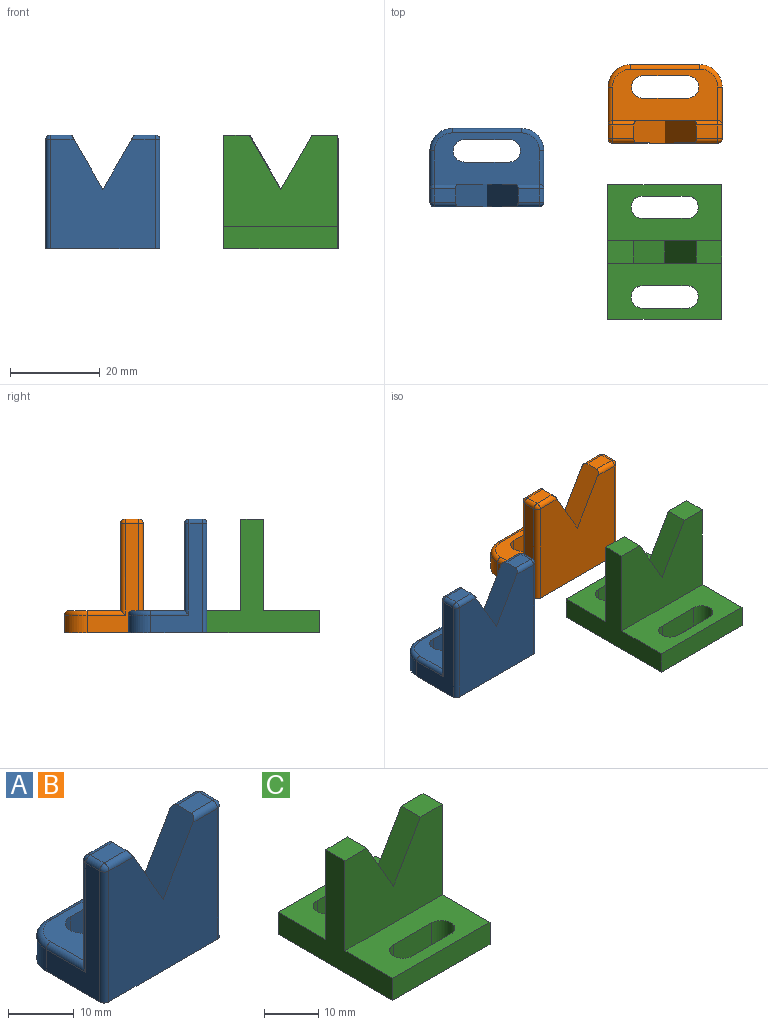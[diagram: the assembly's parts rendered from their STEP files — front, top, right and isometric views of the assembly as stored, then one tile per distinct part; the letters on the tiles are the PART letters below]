
ASSEMBLY  parts=3 mates=2
PART A: 36 faces, bbox 26.2x17.9x25.4 mm
  f0: plane 24.4x11.5mm, normal (-1,0,0), area 107.2mm2, adj f1,f12,f18,f21,f23,f26
  f1: plane 25.4x17.5mm, normal (0,0,-1), area 363.7mm2, adj f0,f2,f7,f9,f10,f11,f12,f13
  f2: plane 24.4x11.5mm, normal (1,0,0), area 107.2mm2, adj f1,f14,f24,f29,f34,f35
  f3: plane 4.72x3mm, normal (0,0,1), area 14.1mm2, adj f4,f25,f29,f30
  f4: plane 12.1x6.99mm, normal (-0.87,0,0.5), area 69.4mm2, adj f3,f5,f7,f8,f25,f30
  f5: plane 12.1x6.99mm, normal (0.87,0,0.5), area 69.4mm2, adj f4,f6,f7,f8,f17,f20
  f6: plane 4.72x3mm, normal (0,0,1), area 14.1mm2, adj f5,f17,f20,f21
  f7: plane 24.4x23.4mm, normal (0,-1,0), area 499.8mm2, adj f1,f4,f5,f17,f18,f24,f25
  f8: plane 23.4x19.4mm, normal (0,1,0), area 382.8mm2, adj f4,f5,f16,f20,f23,f30,f34
  f9: plane 10x5mm, normal (0,-1,0), area 50mm2, adj f1,f10,f15,f16
  f10: cylinder r=2.5mm len=5mm, axis (0,0,-1), area 39.3mm2, adj f1,f9,f11,f16
  f11: plane 10x5mm, normal (0,1,0), area 50mm2, adj f1,f10,f15,f16
  f12: cylinder r=5mm len=5mm, axis (0,0,-1), area 31.4mm2, adj f0,f1,f13,f28
  f13: plane 15.4x4mm, normal (0,1,0), area 61.6mm2, adj f1,f12,f14,f31
  f14: cylinder r=5mm len=5mm, axis (0,0,-1), area 31.4mm2, adj f1,f2,f13,f33
  f15: cylinder r=2.5mm len=5mm, axis (0,0,-1), area 39.3mm2, adj f1,f9,f11,f16
  f16: plane 23.4x11.5mm, normal (0,0,1), area 192.6mm2, adj f8,f9,f10,f11,f15,f26,f28,f31
  f17: cylinder r=1mm len=5.29mm, axis (1,0,0), area 7.7mm2, adj f5,f6,f7,f19
  f18: cylinder r=1mm len=24.4mm, axis (0,0,1), area 38.3mm2, adj f0,f1,f7,f19
  f19: sphere r=1mm, area 1.6mm2, adj f17,f18,f21
  f20: cylinder r=1mm len=5.29mm, axis (-1,0,0), area 7.7mm2, adj f5,f6,f8,f22
  f21: cylinder r=1mm len=3mm, axis (0,1,0), area 4.7mm2, adj f0,f6,f19,f22
  f22: sphere r=1mm, area 1.6mm2, adj f20,f21,f23
  f23: cylinder r=1mm len=20.4mm, axis (0,0,-1), area 31mm2, adj f0,f8,f22,f26
  f24: cylinder r=1mm len=24.4mm, axis (0,0,-1), area 38.3mm2, adj f1,f2,f7,f27
  f25: cylinder r=1mm len=5.29mm, axis (1,0,0), area 7.7mm2, adj f3,f4,f7,f27
  f26: cylinder r=1mm len=8.5mm, axis (0,-1,0), area 12.4mm2, adj f0,f16,f23,f28
  f27: sphere r=1mm, area 1.6mm2, adj f24,f25,f29
  f28: torus R=4mm, axis (0,0,-1), area 11.4mm2, adj f12,f16,f26,f31
  f29: cylinder r=1mm len=3mm, axis (0,1,0), area 4.7mm2, adj f2,f3,f27,f32
  f30: cylinder r=1mm len=5.29mm, axis (-1,0,0), area 7.7mm2, adj f3,f4,f8,f32
  f31: cylinder r=1mm len=15.4mm, axis (-1,0,0), area 24.2mm2, adj f13,f16,f28,f33
  f32: sphere r=1mm, area 1.6mm2, adj f29,f30,f34
  f33: torus R=4mm, axis (0,0,-1), area 11.4mm2, adj f14,f16,f31,f35
  f34: cylinder r=1mm len=20.4mm, axis (0,0,1), area 31mm2, adj f2,f8,f32,f35
  f35: cylinder r=1mm len=8.5mm, axis (0,1,0), area 12.4mm2, adj f2,f16,f33,f34
PART B: same geometry as A
PART C: 21 faces, bbox 25.4x30x25.4 mm
  f0: plane 30x25.4mm, normal (-1,0,0), area 252mm2, adj f1,f6,f7,f8,f9,f14,f18,f20
  f1: plane 30x25.4mm, normal (0,0,-1), area 622.7mm2, adj f0,f2,f9,f10,f11,f12,f13,f15
  f2: plane 30x25.4mm, normal (1,0,0), area 252mm2, adj f1,f3,f7,f8,f9,f14,f18,f20
  f3: plane 5.72x5mm, normal (0,0,1), area 28.6mm2, adj f2,f4,f7,f8
  f4: plane 12.1x6.99mm, normal (-0.87,0,0.5), area 69.9mm2, adj f3,f5,f7,f8
  f5: plane 12.1x6.99mm, normal (0.87,0,0.5), area 69.9mm2, adj f4,f6,f7,f8
  f6: plane 5.72x5mm, normal (0,0,1), area 28.6mm2, adj f0,f5,f7,f8
  f7: plane 25.4x20.4mm, normal (0,-1,0), area 433.7mm2, adj f0,f2,f3,f4,f5,f6,f14
  f8: plane 25.4x20.4mm, normal (0,1,0), area 433.7mm2, adj f0,f2,f3,f4,f5,f6,f20
  f9: plane 25.4x5mm, normal (0,-1,0), area 127mm2, adj f0,f1,f2,f14
  f10: cylinder r=2.5mm len=5mm, axis (0,0,-1), area 39.3mm2, adj f1,f11,f13,f14
  f11: plane 10x5mm, normal (0,1,0), area 50mm2, adj f1,f10,f12,f14
  f12: cylinder r=2.5mm len=5mm, axis (0,0,-1), area 39.3mm2, adj f1,f11,f13,f14
  f13: plane 10x5mm, normal (0,-1,0), area 50mm2, adj f1,f10,f12,f14
  f14: plane 25.4x12.5mm, normal (0,0,1), area 247.9mm2, adj f0,f2,f7,f9,f10,f11,f12,f13
  f15: plane 10x5mm, normal (0,-1,0), area 50mm2, adj f1,f16,f19,f20
  f16: cylinder r=2.5mm len=5mm, axis (0,0,-1), area 39.3mm2, adj f1,f15,f17,f20
  f17: plane 10x5mm, normal (0,1,0), area 50mm2, adj f1,f16,f19,f20
  f18: plane 25.4x5mm, normal (0,1,0), area 127mm2, adj f0,f1,f2,f20
  f19: cylinder r=2.5mm len=5mm, axis (0,0,-1), area 39.3mm2, adj f1,f15,f17,f20
  f20: plane 25.4x12.5mm, normal (0,0,1), area 247.9mm2, adj f0,f2,f8,f15,f16,f17,f18,f19
PLACE A t=(-26,-12.55,19.13)mm
PLACE B t=(13.75,1.68,19.13)mm
PLACE C t=(13.65,-25.12,19.13)mm
MATE planar C.f1 <-> B.f1  axis (0,0,-1) through (13.65,-25.12,-8.17)mm
MATE planar A.f1 <-> B.f1  axis (0,0,-1) through (-26,-7.23,-8.17)mm
